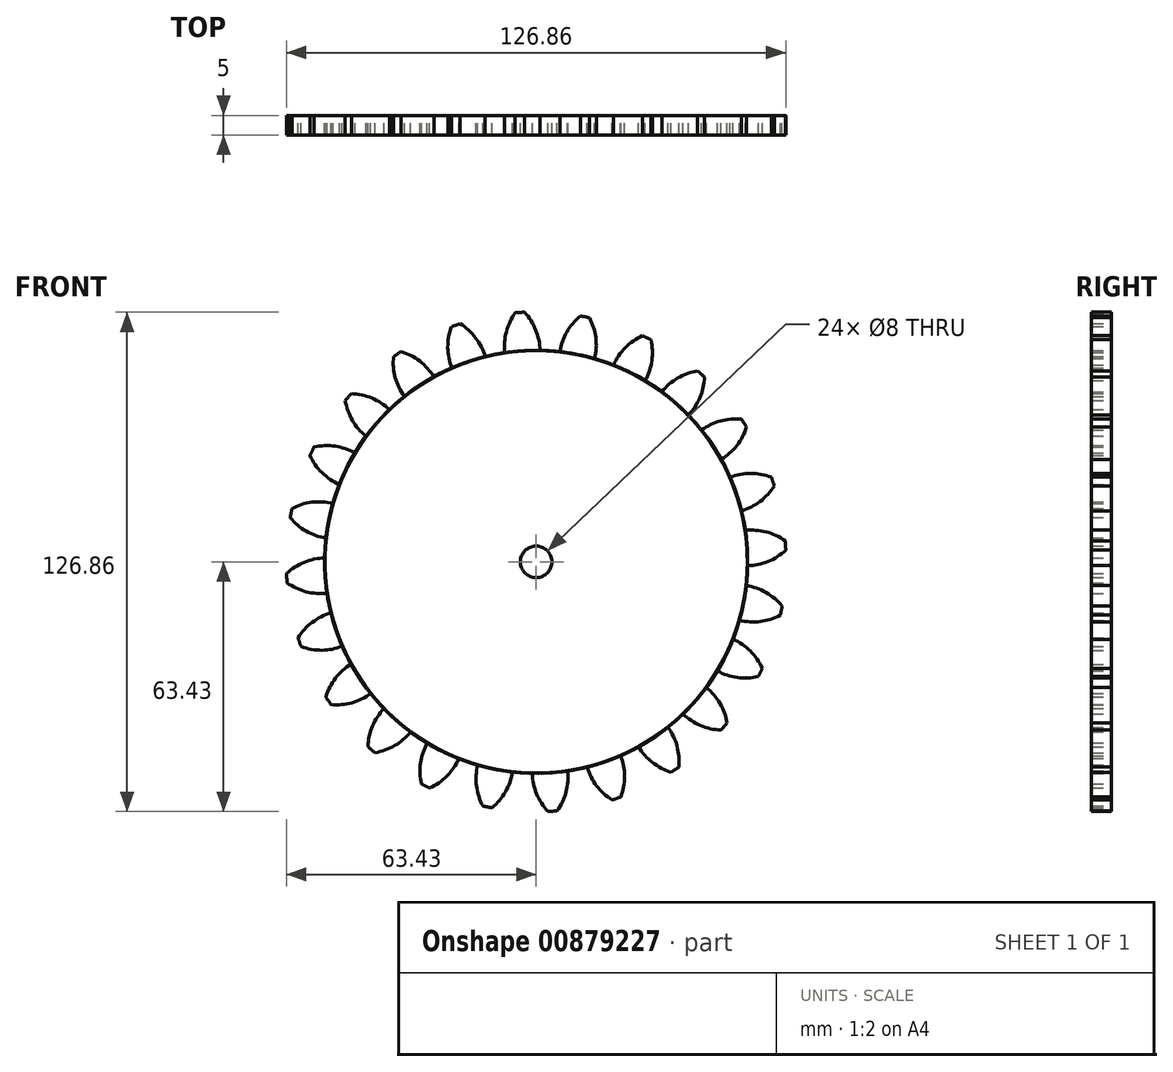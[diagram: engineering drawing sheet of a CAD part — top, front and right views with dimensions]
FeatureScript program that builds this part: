
annotation { "Feature Type Name" : "Feature", "Feature Type Description" : "" }
export const myFeature = defineFeature(function(context is Context, id is Id, definition is map)
    precondition{}
    {
        {
            var Q0;
            Q0=qCreatedBy(makeId("Front.planeOp"),FACE);
            var sketch = newSketch(context, id + "F0", { "sketchPlane" : qUnion([Q0])});
            skCircle(sketch, "E0", {"center": v(0, 0) * mm, "radius": 53.72 * mm});
            skCircle(sketch, "E1", {"center": v(0, 0) * mm, "radius": 58.67 * mm, "construction": true});
            skCircle(sketch, "E2", {"center": v(0, 0) * mm, "radius": 63.5 * mm, "construction": true});
            skLineSegment(sketch, "E3", {"start": v(0, 0) * mm, "end": v(0, 85) * mm, "construction": true});
            skLineSegment(sketch, "E4", {"start": v(0, 0) * mm, "end": v(-5.53, 84.31) * mm, "construction": true});
            skLineSegment(sketch, "E5", {"start": v(0, 58.67) * mm, "end": v(-86.85, 58.67) * mm, "construction": true});
            skLineSegment(sketch, "E6", {"start": v(0, 58.67) * mm, "end": v(-85.06, 27.71) * mm, "construction": true});
            skCircle(sketch, "E7", {"center": v(0, 0) * mm, "radius": 55.14 * mm, "construction": true});
            skCircle(sketch, "E8", {"center": v(0, 58.67) * mm, "radius": 14.6 * mm, "construction": true});
            skArc(sketch, "E9", {"start": v(0.97, 53.71) * mm, "mid": v(-0.1, 58.94) * mm, "end": v(-2.99, 63.43) * mm});
            skArc(sketch, "E10.MirrorCS", {"start": v(-7.98, 53.13) * mm, "mid": v(-7.59, 58.45) * mm, "end": v(-5.32, 63.28) * mm});
            skArc(sketch, "E11", {"start": v(-2.99, 63.43) * mm, "mid": v(-4.15, 63.36) * mm, "end": v(-5.32, 63.28) * mm});
            skCircle(sketch, "E12", {"center": v(0, 0) * mm, "radius": 4 * mm});
            skSolve(sketch);
        }
        {
            var Q0;
            {var subQ0=sQuery(id+"F0.wireOp",EDGE,"E0");var subQ1=makeQuery(id+"F0.imprint","INTERSECT",VERTEX,{"derivedFrom":[subQ0,sQuery(id+"F0.wireOp",EDGE,"E9")]});Q0=makeQuery(id+"F0.imprint","IMPRINT",FACE,{"disambiguationData":[TD([[makeQuery(id+"F0.imprint","IMPRINT",EDGE,{"disambiguationData":[TD([[subQ1,-1.0]])],"derivedFrom":subQ0}),1.0]])]});}
            var Q1;
            {var subQ0=sQuery(id+"F0.wireOp",EDGE,"E9");Q1=makeQuery(id+"F0.imprint","IMPRINT",FACE,{"disambiguationData":[TD([[makeQuery(id+"F0.imprint","IMPRINT",EDGE,{"derivedFrom":subQ0}),1.0]])]});}
            extrude(context, id + "F1", {"entities" : qUnion([Q0, Q1]), "depth" : 5 * mm, "offsetDistance" : 25 * mm});
        }
        {
            var Q0;
            Q0=makeQuery(id+"F1.opExtrude","SWEPT_BODY",BODY,{"disambiguationData":[OSD([sQuery(id+"F0.wireOp",EDGE,"E0"),sQuery(id+"F0.wireOp",EDGE,"E9"),sQuery(id+"F0.wireOp",EDGE,"E10.MirrorCS"),sQuery(id+"F0.wireOp",EDGE,"E11")])]});
            var Q1;
            Q1=makeQuery(id+"F1.opExtrude","SWEPT_FACE",FACE,{"disambiguationData":[OSD([sQuery(id+"F0.wireOp",EDGE,"E0")])]});
            circularPattern(context, id + "F2", {"entities" : qUnion([Q0]), "axis" : qUnion([Q1]), "angle" : 360 * degree, "instanceCount" : 24, "equalSpace" : true});
        }
    });
